# Revit family: Gira_543000
name_source: partatom
category: Electrical Fixtures
revit_build: Autodesk Revit 2017 (Build: 20160225_1515(x64)
units: mm (PartAtom-declared; Revit-internal decimal feet)

## family parameters
Cut with Voids When Loaded = No
Host = Face
Maintain Annotation Orientation = No
Part Type = Normal
Room Calculation Point = No
Round Connector Dimension = Use Diameter
Shared = No

## types (1)
- WL dimm.act. 1-g DRA Gira eNet
    App control via Bluetooth = No
    Applicable with button = No
    Applicable with infrared button = No
    Applicable with movement sensor = No
    Applicable with presence indicator = No
    Applicable with time switch/timer = No
    Applicable with transmission button = No
    BIM = https://media.live.bim.site X1 REG KNX.rfa
    BIMSITE_PRODUCT_ID = a9636d8d94fcf1a9dfd08dc613c52d40db9e02c7
    Bus connection included = No
    Cost = 0 $
    Default Elevation = 1219 mm
    Description = WL dimm.act.1g DRA eNet eNet wireless dimming actuator, 1-gang 20 - 500 W VA DRA Features: Can be set with eNet server:: - Fully encrypted wireless transmission (AES CCM) from eNet Server software version 2.0. - Operation locks. - Device software update. - The eNet wireless dimming actuator receives telegrams for switching and dimming various electrical loads from the eNet wireless reception module or eNet server via a data cable. - Switching and dimming light bulbs, HV halogen lamps, electronic transformers for halogen or LED lamps, dimmable inductive transformers for halogen or LED lamps, HV LED or compact fluorescent lamps. - Bulb-saving switch-on. - Switch-on and minimum brightness can be saved. - Scene operation. - Status display with LED. - Status feedback to eNet wireless sensors. - Short-circuit and excess-temperature protection. - Automatic or manual setting of dimming process. Can be set with eNet server:: - Maximum brightness. - Dimming process. - Dimming speed. - Delay time. - Switch-on off delay. - Dimming ramp up down. - Switch-off pre-warning. - Permanent-on, permanent-off. - Hotel function. - Light control.,Notes : - An eNet wireless reception module or an eNet server is required to operate this DIN-rail mounting device.
    Dimming phase cut-off = No
    Dimming phase cut-on = No
    GTIN = 4010337774259
    HAN = 543000
    Halogen free = No
    HeinzeBIM = https://www.heinze.de
    Light value memory = No
    Local operation/hand operation = No
    Manufacturer = Gira
    Model = Dimming actuator
    Number of inputs = 0
    Number of outputs = 1
    Output power [Voltampere] = [500:500]
    Parallel-service possible = No
    Power boost suitable = No
    Radio frequent bidirectional = No
    Serial dimmer = No
    Transparent = No
    Type of load = Universal
    URL = https://www.gira.de
    With label area = No

## geometry (parser evidence)
native form markers: Blend x2, Sweep x3
no freeform markers — native parametric forms only
